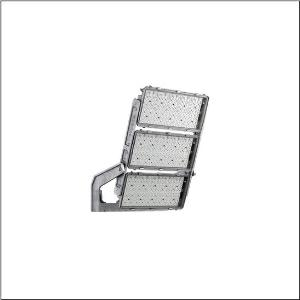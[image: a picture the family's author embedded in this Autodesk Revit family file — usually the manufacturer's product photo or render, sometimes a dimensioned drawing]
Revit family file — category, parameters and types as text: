
# Revit family: floodlight_fl_11_maxi_pro_remote___pl43_5xa779425a01aa_2185
name_source: partatom
category: Lighting Fixtures
units: mm (PartAtom-declared; Revit-internal decimal feet)

## family parameters
Cut with Voids When Loaded = No
Host = Face
Light Source = No
Part Type = Normal
Room Calculation Point = No
Round Connector Dimension = Use Diameter
Shared = No

## types (1)
- --- (1 x LED, 162210 lm, 1334.7 W, 3000K)
    Apparent Load = 1335 VA
    CIE Flux Codes = 25 74 99 100 100
    Color Rendering = 70
    Color Temperature = 3000K
    Default Elevation = 1800 mm
    Description = Floodlight FL 11  maxi  pro Remote floodlight; light control with lens of PMMA; cover panel of toughened safety glass, transparent; light distribution: PL43, asymmetric direct distribution, LEDcolour temperature: 3000K, rated luminous flux: 162.210lm, colour rendering: CRI > 70, light colour: 730; luminous efficacy: 122lm/W; brightness control: DALI 2 (1 DALI address); with terminal, 8-pole, max. 2.5mm², mains connection: 220..240V/380..400V AC, 50/60Hz, surge voltage resistance: line to ground: 10kV, ECG replaceable separately, LED unit replaceable without ESD environment, dustproof LED module, dimming range 10..100%, no afterglow with DALI off / DMX off command; 1335W floodlight with 2x LED unit of diecast aluminium, coated grey; length: 713mm / width: 651mm / height: 338mm; mounting bracket, of diecast aluminium, uncoated, natural, equipment: Power, protection rating (complete): IP66; insulation class (complete): insulation class I (protective earthing); certification: CE, ENEC, VDE; ball protection: ball impact resistance with accessories, impact resistance: IK07; rated ambient temperature 10°C, only for outdoor installations, permissible operating ambient temperature: -40..+30°C, permissible storage temperature: -40..+85°C; packaging unit: 1 piece

Light Distribution: PL43
    Height = 320 mm
    Lamp = 1 x LED
    Lamp Light Flux = 162210 lm
    Lamp Power = 1334.7 W
    Lamp count = 1
    Length = 1002 mm
    Luminous efficacy = 122 lm/W
    Manufacturer = Siteco
    ModVariant = No
    Model = 5XA779425A01AA
    Mounting Place = Ceiling
    Mounting Type = Surface mounted
    Number of Poles = 1
    OnlyDefault = Yes
    Power Factor = 1
    Product Name = Floodlight FL 11 maxi pro Remote | PL43
    Product group = floodlight | ceiling mounted
    ProductGroupID = 303
    Protection Class = Protection class I
    Protection Degree = IP 66
    RLX_Detail_Level = 1
    RLX_Emergency_Light_Flux = 0 lm
    RLX_Emergency_Type = 0
    RLX_Emergency_Type_DB = No
    RlxData = <blob elided: 52445 chars, md5=8ed4ee8c>
    Socket = socket
    Standby Power = 0 W
    System Light Flux = 162210 lm
    System Power = 1335 W
    Type Comments = factory setting: luminous flux: 100 % | dim-lin: 254 | 920 mA
    Type Image = l_1006784.jpg
    URL = http://relux.com
    VarID = @adj_044879
    Voltage = 0 V
    Weight = 0.00 kg
    Width = 655 mm

## geometry (parser evidence)
native form markers: Blend x4, Sweep x14
no freeform markers — native parametric forms only
